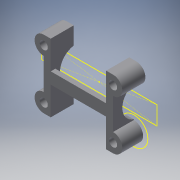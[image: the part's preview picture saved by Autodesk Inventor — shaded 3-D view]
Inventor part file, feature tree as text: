
AUTODESK INVENTOR PART (.ipt)
format: ipt  version: 2019 (Build 230136000, 136)  size: 276,480 bytes
history: native  units: mm
features: sketch x10, other x6, extrude x5, projected_geometry x3, fillet x2
ambient origin geometry x8: Origin, YZ Plane, XZ Plane, XY Plane, X Axis, Y Axis, Z Axis, Center Point
bodies: Body1 (feature_tree)
feature tree (26):
  other  "Fastening.ipt"
  extrude  "Выдавливание1"  Depth=10.0mm
  extrude  "Выдавливание2"  Depth=1.0mm TaperAngle=0.0deg
  extrude  "Выдавливание3"  Depth=12.0mm
  extrude  "Выдавливание4"  Depth=3.0mm TaperAngle=0.0deg
  other  "Непосредственное редактирование1"
  extrude  "Выдавливание5"  Depth=2.0mm
  fillet  "Сопряжение1"  Radius=2.0mm
  fillet  "Сопряжение2"  Radius=5.0mm
  other  "Твердое тело1::Fastening.ipt"
  other  "Элемент создания тегов1"
  sketch  "Эскиз1"
  sketch  "Эскиз2"
  sketch  "Эскиз3"
  sketch  "Эскиз5"
  sketch  "Эскиз6"
  sketch  "Эскиз7"
  sketch  "Эскиз8"
  sketch  "Эскиз9"
  sketch  "Эскиз10"
  projected_geometry  "Спроецированная петля1"
  sketch  "Эскиз11"
  projected_geometry  "Спроецированная петля2"
  projected_geometry  "Спроецированная петля3"
  other  "Твердое тело1"
  other  "Перенос1"
